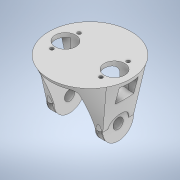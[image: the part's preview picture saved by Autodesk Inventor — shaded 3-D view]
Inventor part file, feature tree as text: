
AUTODESK INVENTOR PART (.ipt)
format: ipt  version: 2020 (Build 240168000, 168)  size: 347,648 bytes
history: native  units: in
note: dims shown in document units (in); Inventor stores cm internally (conversion verified against a paired STEP export)
features: sketch x10, extrude x9, plane x1, loft x1, mirror x1, fillet x1
ambient origin geometry x8: Origin, YZ Plane, XZ Plane, XY Plane, X Axis, Y Axis, Z Axis, Center Point
bodies: Body1 (feature_tree)
feature tree (23):
  sketch  "Sketch5"  dims[d21=-2.205in d22=0.0in d23=90.0deg]
  plane  "Work Plane1"
  loft  "Loft1"
  extrude  "Extrusion4"  Depth=4.0in
  extrude  "Extrusion5"  Depth=2.75in TaperAngle=0.0deg
  extrude  "Extrusion6"  Depth=0.11in TaperAngle=0.0deg
  mirror  "Mirror1"
  extrude  "Extrusion7"  Depth=0.199in TaperAngle=0.0deg
  extrude  "Extrusion8"  Depth=2.0in
  extrude  "Extrusion9"  Depth=2.4in
  extrude  "Extrusion10"  Depth=1.0in
  sketch  "Sketch14"  dims[d48=2.4in d51=0.0in d52=0.0in d53=0.0625in d54=1.0in d55=0.0in d56=0.17in d57=1.0in d58=0.0in d59=0.25in]
  extrude  "Extrusion11"  Depth=1.5in
  extrude  "Extrusion12"  TaperAngle=0.0deg  [1 undecoded]
  fillet  "Fillet1"  Radius=0.0625in
  sketch  "Sketch6"  dims[d24=0.0in d25=90.0deg d26=4.0in]
  sketch  "Sketch7"  dims[d27=2.75in d28=2.75in d29=0.0in]
  sketch  "Sketch8"  dims[d30=0.5in d31=0.11in d32=0.0in]
  sketch  "Sketch9"  dims[d33=1.0in d34=0.199in d35=0.0in]
  sketch  "Sketch10"  dims[d36=2.0in d38=2.0in]
  sketch  "Sketch11"  dims[d39=1.81in d40=0.0in d41=2.4in]
  sketch  "Sketch12"  dims[d42=1.0in d43=0.0in d44=1.0in]
  sketch  "Sketch13"  dims[d45=2.893in d46=0.0in d47=1.5in]
note: 1 required parameter value undecoded (feature->parameter linkage not recoverable at this tier; creation-order binding heuristic only, values carry confidence <= 0.55)
